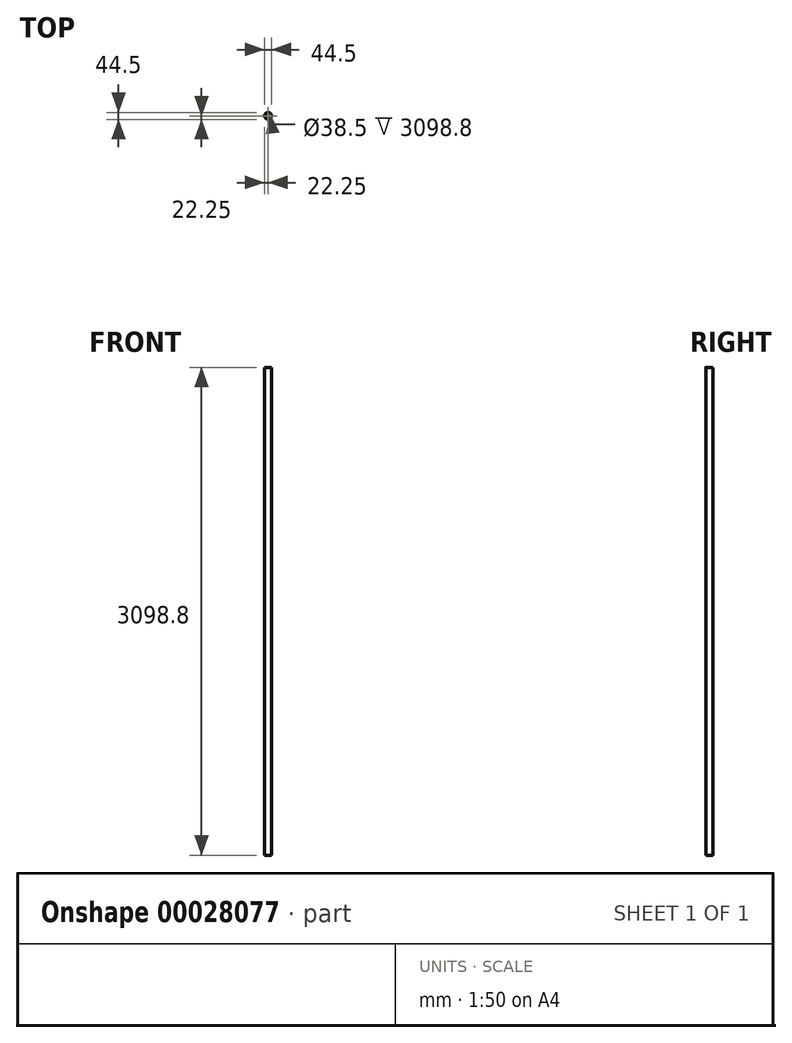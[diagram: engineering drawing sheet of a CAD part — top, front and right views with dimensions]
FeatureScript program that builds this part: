
annotation { "Feature Type Name" : "Feature", "Feature Type Description" : "" }
export const myFeature = defineFeature(function(context is Context, id is Id, definition is map)
    precondition{}
    {
        {
            var Q0;
            Q0=qCreatedBy(makeId("Top.planeOp"),FACE);
            var sketch = newSketch(context, id + "F0", { "sketchPlane" : qUnion([Q0])});
            skCircle(sketch, "E0", {"center": v(0, 0) * mm, "radius": 22.25 * mm});
            skCircle(sketch, "E1.0", {"center": v(0, 0) * mm, "radius": 19.25 * mm});
            skSolve(sketch);
        }
        {
            var Q0;
            Q0=makeQuery(id+"F0.imprint","IMPRINT",FACE,{"disambiguationData":[TD([[makeQuery(id+"F0.imprint","IMPRINT",EDGE,{"derivedFrom":sQuery(id+"F0.wireOp",EDGE,"E0")}),1.0]])]});
            extrude(context, id + "F1", {"entities" : qUnion([Q0]), "oppositeDirection" : true, "depth" : 3098.8 * mm});
        }
    });
